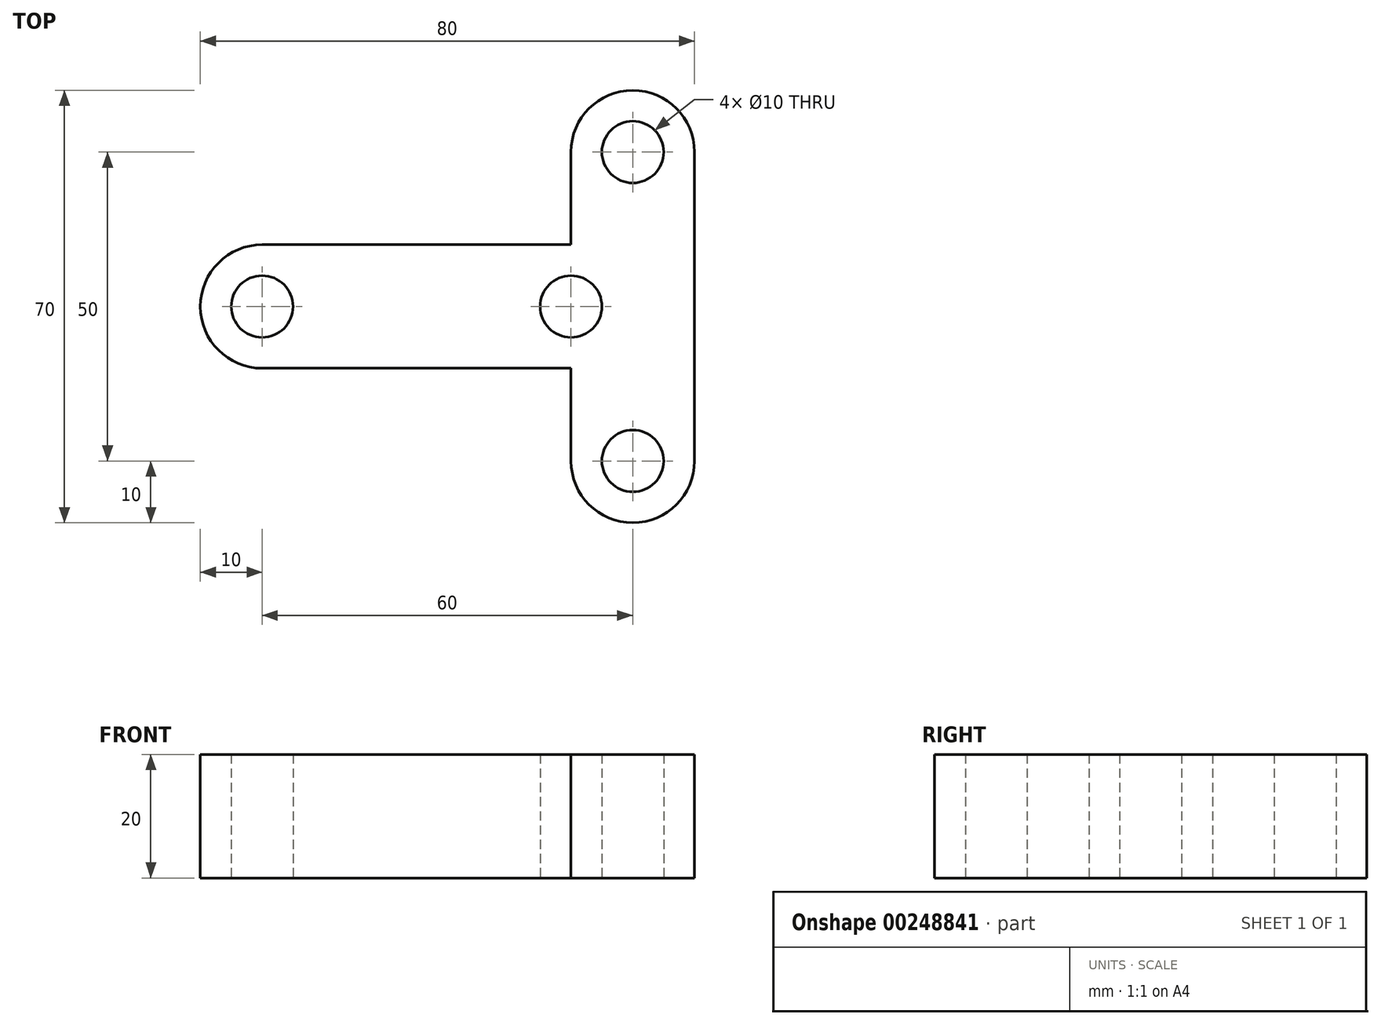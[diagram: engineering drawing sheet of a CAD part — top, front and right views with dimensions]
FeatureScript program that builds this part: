
annotation { "Feature Type Name" : "Feature", "Feature Type Description" : "" }
export const myFeature = defineFeature(function(context is Context, id is Id, definition is map)
    precondition{}
    {
        {
            var Q0;
            Q0=qCreatedBy(makeId("Top.planeOp"),FACE);
            var sketch = newSketch(context, id + "F0", { "sketchPlane" : qUnion([Q0])});
            skLineSegment(sketch, "E0.bottom", {"start": v(25, 10) * mm, "end": v(-25, 10) * mm});
            skLineSegment(sketch, "E0.top", {"start": v(25, -10) * mm, "end": v(-25, -10) * mm});
            skPoint(sketch, "E0.middle", {"position": v(0, 0) * mm});
            skLineSegment(sketch, "E1.right", {"start": v(45, 25) * mm, "end": v(45, -25) * mm});
            skCircle(sketch, "E2", {"center": v(-25, 0) * mm, "radius": 5 * mm});
            skCircle(sketch, "E3", {"center": v(35, -25) * mm, "radius": 5 * mm});
            skCircle(sketch, "E4", {"center": v(35, 25) * mm, "radius": 5 * mm});
            skCircle(sketch, "E5", {"center": v(25, 0) * mm, "radius": 5 * mm});
            skLineSegment(sketch, "E6", {"start": v(25, 25) * mm, "end": v(25, 10) * mm});
            skLineSegment(sketch, "E7", {"start": v(25, -10) * mm, "end": v(25, -25) * mm});
            skLineSegment(sketch, "E8", {"start": v(45, -25) * mm, "end": v(45, 25) * mm});
            skArc(sketch, "E9", {"start": v(25, 25) * mm, "mid": v(35, 35) * mm, "end": v(45, 25) * mm});
            skArc(sketch, "E10", {"start": v(25, -25) * mm, "mid": v(35, -35) * mm, "end": v(45, -25) * mm});
            skArc(sketch, "E11", {"start": v(-25, -10) * mm, "mid": v(-35, 0) * mm, "end": v(-25, 10) * mm});
            skLineSegment(sketch, "E12", {"start": v(-25, -10) * mm, "end": v(25, -10) * mm});
            skSolve(sketch);
        }
        {
            var Q0;
            Q0=makeQuery(id+"F0.imprint","IMPRINT",FACE,{"disambiguationData":[TD([[makeQuery(id+"F0.imprint","IMPRINT",EDGE,{"derivedFrom":sQuery(id+"F0.wireOp",EDGE,"E0.bottom")}),1.0]])]});
            extrude(context, id + "F1", {"entities" : qUnion([Q0]), "endBound" : BoundingType.SYMMETRIC, "depth" : 20 * mm});
        }
    });
